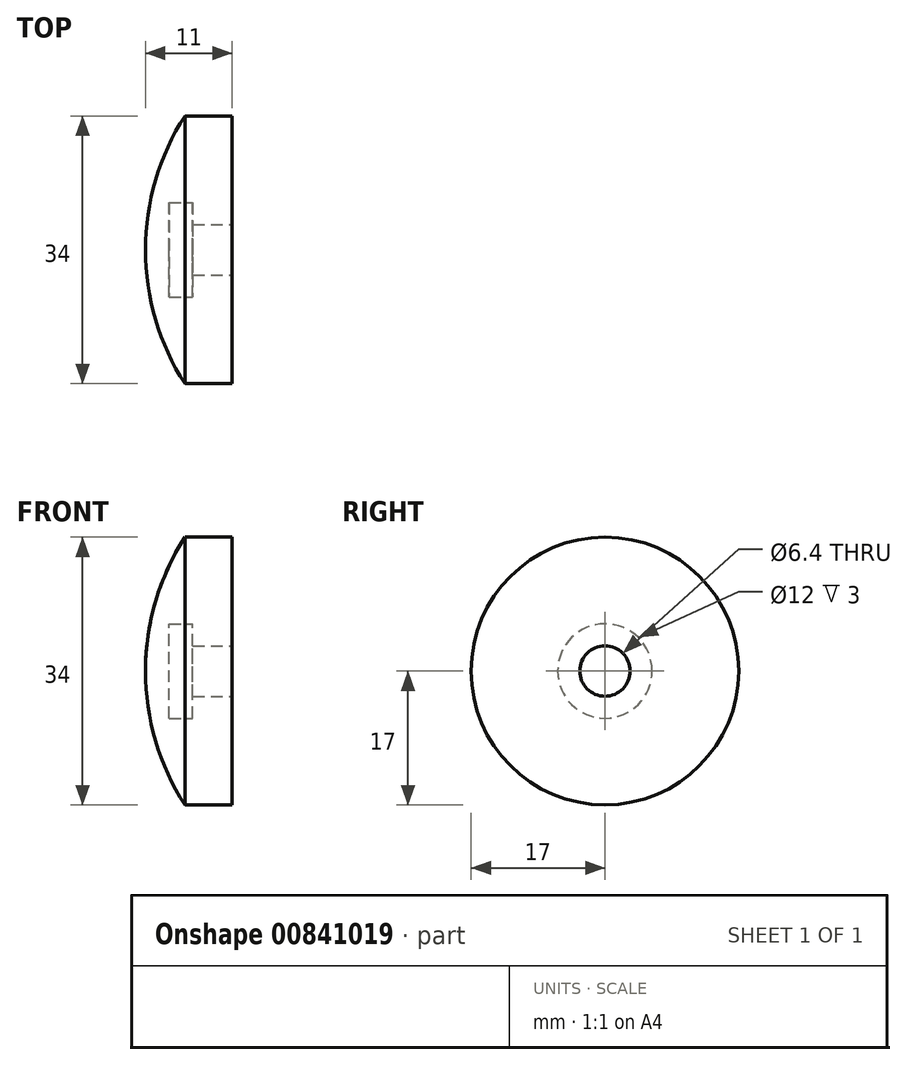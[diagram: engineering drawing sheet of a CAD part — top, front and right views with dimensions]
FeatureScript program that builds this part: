
annotation { "Feature Type Name" : "Feature", "Feature Type Description" : "" }
export const myFeature = defineFeature(function(context is Context, id is Id, definition is map)
    precondition{}
    {
        {
            var Q0;
            Q0=qCreatedBy(makeId("Front.planeOp"),FACE);
            var sketch = newSketch(context, id + "F0", { "sketchPlane" : qUnion([Q0])});
            skLineSegment(sketch, "E0.bottom", {"start": v(0, 0) * mm, "end": v(-11, 0) * mm});
            skLineSegment(sketch, "E0.top", {"start": v(0, 17) * mm, "end": v(-6, 17) * mm});
            skLineSegment(sketch, "E0.left", {"start": v(0, 0) * mm, "end": v(0, 17) * mm});
            skArc(sketch, "E1", {"start": v(-6, 17) * mm, "mid": v(-9.72, 8.86) * mm, "end": v(-11, 0) * mm});
            skLineSegment(sketch, "E2", {"start": v(-11, 0) * mm, "end": v(-11, 19.88) * mm, "construction": true});
            skLineSegment(sketch, "E3", {"start": v(-8, 0) * mm, "end": v(-8, 6) * mm});
            skLineSegment(sketch, "E4", {"start": v(-8, 6) * mm, "end": v(-5, 6) * mm});
            skLineSegment(sketch, "E5", {"start": v(-5, 6) * mm, "end": v(-5, 3.2) * mm});
            skLineSegment(sketch, "E6", {"start": v(-5, 3.2) * mm, "end": v(0, 3.2) * mm});
            skSolve(sketch);
        }
        {
            var Q0;
            {var subQ2=sQuery(id+"F0.wireOp",EDGE,"E0.top");Q0=makeQuery(id+"F0.imprint","IMPRINT",FACE,{"disambiguationData":[TD([[makeQuery(id+"F0.imprint","IMPRINT",EDGE,{"derivedFrom":subQ2}),1.0]])]});}
            var Q1;
            Q1=sQuery(id+"F0.wireOp",EDGE,"E0.bottom");
            revolve(context, id + "F1", {"surfaceOperationType" : NewSurfaceOperationType.NEW, "entities" : qUnion([Q0]), "axis" : qUnion([Q1]), "revolveType" : RevolveType.FULL});
        }
    });
